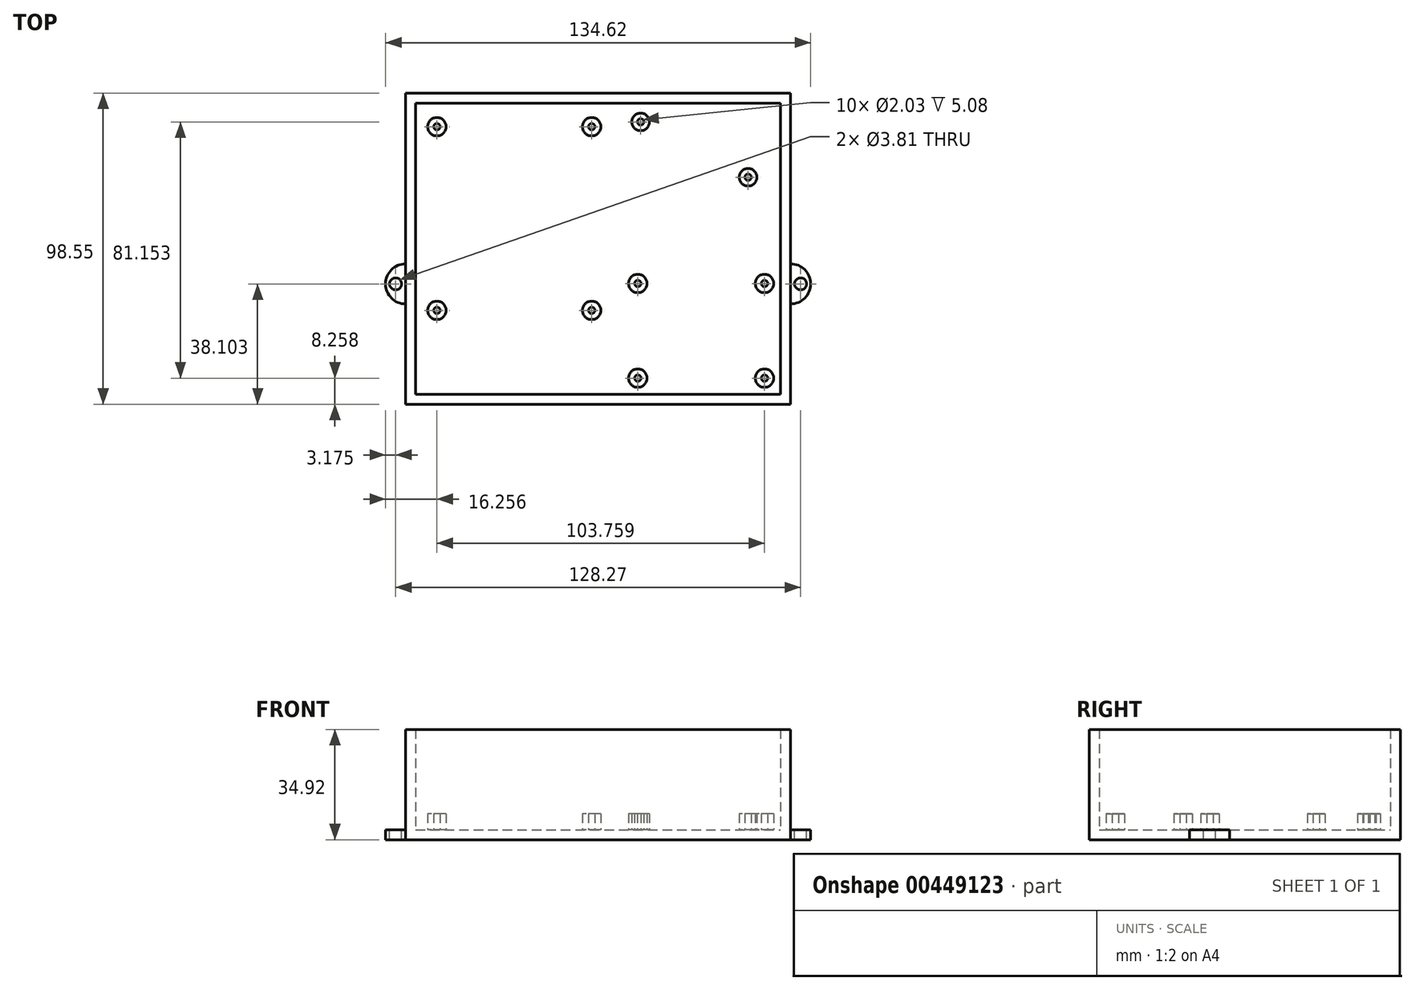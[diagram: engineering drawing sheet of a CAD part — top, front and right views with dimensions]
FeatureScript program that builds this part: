
annotation { "Feature Type Name" : "Feature", "Feature Type Description" : "" }
export const myFeature = defineFeature(function(context is Context, id is Id, definition is map)
    precondition{}
    {
        {
            var Q0;
            Q0=qCreatedBy(makeId("Top.planeOp"),FACE);
            var sketch = newSketch(context, id + "F0", { "sketchPlane" : qUnion([Q0])});
            skLineSegment(sketch, "E0.bottom", {"start": v(-73.66, 41.28) * mm, "end": v(48.26, 41.28) * mm});
            skLineSegment(sketch, "E0.top", {"start": v(-73.66, -57.28) * mm, "end": v(48.26, -57.28) * mm});
            skLineSegment(sketch, "E0.left", {"start": v(-73.66, 41.28) * mm, "end": v(-73.66, -57.28) * mm});
            skLineSegment(sketch, "E0.right", {"start": v(48.26, 41.28) * mm, "end": v(48.26, -57.28) * mm});
            skSolve(sketch);
        }
        {
            var Q0;
            Q0=makeQuery(id+"F0.imprint","IMPRINT",FACE,{"disambiguationData":[TD([[makeQuery(id+"F0.imprint","IMPRINT",EDGE,{"derivedFrom":sQuery(id+"F0.wireOp",EDGE,"E0.bottom")}),-1.0]])]});
            extrude(context, id + "F1", {"entities" : qUnion([Q0]), "depth" : 3.17 * mm});
        }
        {
            var Q0;
            Q0=makeQuery(id+"F1.opExtrude","SWEPT_FACE",FACE,{"disambiguationData":[OSD([sQuery(id+"F0.wireOp",EDGE,"E0.right")])]});
            var sketch = newSketch(context, id + "F2", { "sketchPlane" : qUnion([Q0])});
            skLineSegment(sketch, "E1.bottom", {"start": v(-25.53, 0) * mm, "end": v(-12.83, 0) * mm});
            skLineSegment(sketch, "E1.top", {"start": v(-25.53, 3.17) * mm, "end": v(-12.83, 3.17) * mm});
            skLineSegment(sketch, "E1.left", {"start": v(-25.53, 0) * mm, "end": v(-25.53, 3.17) * mm});
            skLineSegment(sketch, "E1.right", {"start": v(-12.83, 0) * mm, "end": v(-12.83, 3.17) * mm});
            skLineSegment(sketch, "E2", {"start": v(-25.53, 0) * mm, "end": v(-57.28, 0) * mm, "construction": true});
            skSolve(sketch);
        }
        {
            var Q0;
            Q0=makeQuery(id+"F2.imprint","IMPRINT",FACE,{"disambiguationData":[TD([[makeQuery(id+"F2.imprint","IMPRINT",EDGE,{"derivedFrom":sQuery(id+"F2.wireOp",EDGE,"E1.bottom")}),-1.0]])]});
            extrude(context, id + "F3", {"entities" : qUnion([Q0]), "operationType" : NewBodyOperationType.ADD, "depth" : 6.35 * mm});
        }
        {
            var Q0;
            Q0=makeQuery(id+"F1.opExtrude","SWEPT_FACE",FACE,{"disambiguationData":[OSD([sQuery(id+"F0.wireOp",EDGE,"E0.left")])]});
            var sketch = newSketch(context, id + "F4", { "sketchPlane" : qUnion([Q0])});
            skLineSegment(sketch, "E3.bottom", {"start": v(12.83, 0) * mm, "end": v(25.53, 0) * mm});
            skLineSegment(sketch, "E3.top", {"start": v(12.83, 3.18) * mm, "end": v(25.53, 3.18) * mm});
            skLineSegment(sketch, "E3.left", {"start": v(12.83, 0) * mm, "end": v(12.83, 3.18) * mm});
            skLineSegment(sketch, "E3.right", {"start": v(25.53, 0) * mm, "end": v(25.53, 3.18) * mm});
            skLineSegment(sketch, "E4", {"start": v(57.28, 0) * mm, "end": v(25.53, 0) * mm, "construction": true});
            skSolve(sketch);
        }
        {
            var Q0;
            Q0=makeQuery(id+"F4.imprint","IMPRINT",FACE,{"disambiguationData":[TD([[makeQuery(id+"F4.imprint","IMPRINT",EDGE,{"derivedFrom":sQuery(id+"F4.wireOp",EDGE,"E3.bottom")}),1.0]])]});
            extrude(context, id + "F5", {"entities" : qUnion([Q0]), "operationType" : NewBodyOperationType.ADD, "depth" : 6.35 * mm});
        }
        {
            var Q0;
            Q0=makeQuery(id+"FaVg6euIrQHNksh_1.opExtrude","CAP_EDGE",EDGE,{"disambiguationData":[OSD([sQuery(id+"FkQ3vqy4hY3QKMT_1.wireOp",EDGE,"Yg9sziPS-2V4h-UQLX-E8gU-2OajwgteZGGz.right")])],"isStart":false});
            var Q1;
            Q1=makeQuery(id+"FaVg6euIrQHNksh_1.opExtrude","CAP_EDGE",EDGE,{"disambiguationData":[OSD([sQuery(id+"FkQ3vqy4hY3QKMT_1.wireOp",EDGE,"Yg9sziPS-2V4h-UQLX-E8gU-2OajwgteZGGz.left")])],"isStart":false});
            var Q2;
            Q2=makeQuery(id+"FaVg6euIrQHNksh_1.opExtrude","CAP_EDGE",EDGE,{"disambiguationData":[OSD([sQuery(id+"FkQ3vqy4hY3QKMT_1.wireOp",EDGE,"JQurt5le-ksY8-GB8i-C2E5-fmt823hqq3je.right")])],"isStart":false});
            var Q3;
            Q3=makeQuery(id+"FaVg6euIrQHNksh_1.opExtrude","CAP_EDGE",EDGE,{"disambiguationData":[OSD([sQuery(id+"FkQ3vqy4hY3QKMT_1.wireOp",EDGE,"JQurt5le-ksY8-GB8i-C2E5-fmt823hqq3je.left")])],"isStart":false});
            var Q4;
            Q4=makeQuery(id+"F5.opExtrude","CAP_EDGE",EDGE,{"disambiguationData":[OSD([sQuery(id+"F4.wireOp",EDGE,"E3.right")])],"isStart":false});
            var Q5;
            Q5=makeQuery(id+"F5.opExtrude","CAP_EDGE",EDGE,{"disambiguationData":[OSD([sQuery(id+"F4.wireOp",EDGE,"E3.left")])],"isStart":false});
            var Q6;
            Q6=makeQuery(id+"F3.opExtrude","CAP_EDGE",EDGE,{"disambiguationData":[OSD([sQuery(id+"F2.wireOp",EDGE,"E1.left")])],"isStart":false});
            var Q7;
            Q7=makeQuery(id+"F3.opExtrude","CAP_EDGE",EDGE,{"disambiguationData":[OSD([sQuery(id+"F2.wireOp",EDGE,"E1.right")])],"isStart":false});
            fillet(context, id + "F6", {"entities" : qUnion([Q0, Q1, Q2, Q3, Q4, Q5, Q6, Q7]), "radius" : 6.35 * mm, "tangentPropagation" : true, "allowEdgeOverflow" : false});
        }
        {
            var Q0;
            {var subQ2=sQuery(id+"FBJeiMYnQQNTDJ8_1.wireOp",EDGE,"NU6RmQLN-OpBs-DRR8-WLyE-sT2VYZkfqMhq.right");var subQ3=makeQuery(id+"F1.opExtrude","SWEPT_FACE",FACE,{"disambiguationData":[OSD([subQ2])]});var subQ5=sQuery(id+"F2.wireOp",EDGE,"E1.top");var subQ11=sQuery(id+"FBJeiMYnQQNTDJ8_1.wireOp",EDGE,"NU6RmQLN-OpBs-DRR8-WLyE-sT2VYZkfqMhq.left");var subQ12=sQuery(id+"FBJeiMYnQQNTDJ8_1.wireOp",EDGE,"NU6RmQLN-OpBs-DRR8-WLyE-sT2VYZkfqMhq.bottom");var subQ13=sQuery(id+"FBJeiMYnQQNTDJ8_1.wireOp",EDGE,"NU6RmQLN-OpBs-DRR8-WLyE-sT2VYZkfqMhq.top");var subQ14=sQuery(id+"F4.wireOp",EDGE,"E3.top");Q0=makeQuery(id+"Fuqd1rwQzSbVv2O_1.boolean.opBoolean","SPLIT",FACE,{"disambiguationData":[TD([subQ3])],"derivedFrom":makeQuery(id+"F2G8V8C4itq5gVN_1.boolean.opBoolean","SPLIT",FACE,{"disambiguationData":[TD([makeQuery(id+"FTzhnSVDk6kkX89_0.opExtrude","SWEPT_FACE",FACE,{"disambiguationData":[OSD([sQuery(id+"F0IJRBmxtiezRhW_0.wireOp",EDGE,"C5BwnNIY-jE5H-Hf46-yxJA-r1WcZ6m8hW8I.bottom")])]})])],"derivedFrom":makeQuery(id+"F5.boolean.opBoolean","MERGE",FACE,{"derivedFrom":[makeQuery(id+"F3.boolean.opBoolean","MERGE",FACE,{"derivedFrom":[makeQuery(id+"F1.opExtrude","CAP_FACE",FACE,{"disambiguationData":[OSD([subQ12,subQ13,subQ11,subQ2])],"isStart":false}),makeQuery(id+"F3.opExtrude","SWEPT_FACE",FACE,{"disambiguationData":[OSD([subQ5])]})]}),makeQuery(id+"F5.opExtrude","SWEPT_FACE",FACE,{"disambiguationData":[OSD([subQ14])]})]})})});}
            var sketch = newSketch(context, id + "F7", { "sketchPlane" : qUnion([Q0])});
            skCircle(sketch, "E5", {"center": v(51.44, -19.18) * mm, "radius": 1.9 * mm});
            skLineSegment(sketch, "E6", {"start": v(-80, -19.18) * mm, "end": v(-73.66, -19.18) * mm, "construction": true});
            skCircle(sketch, "E7", {"center": v(-76.83, -19.18) * mm, "radius": 1.9 * mm});
            skLineSegment(sketch, "E8", {"start": v(54.61, -19.18) * mm, "end": v(48.26, -19.18) * mm, "construction": true});
            skLineSegment(sketch, "E9", {"start": v(48.26, -12.83) * mm, "end": v(48.26, -25.53) * mm, "construction": true});
            skSolve(sketch);
        }
        {
            var Q0;
            Q0=makeQuery(id+"F7.imprint","IMPRINT",FACE,{"disambiguationData":[TD([[makeQuery(id+"F7.imprint","IMPRINT",EDGE,{"derivedFrom":sQuery(id+"F7.wireOp",EDGE,"E7")}),1.0]])]});
            var Q1;
            Q1=makeQuery(id+"F7.imprint","IMPRINT",FACE,{"disambiguationData":[TD([[makeQuery(id+"F7.imprint","IMPRINT",EDGE,{"derivedFrom":sQuery(id+"F7.wireOp",EDGE,"E5")}),1.0]])]});
            extrude(context, id + "F8", {"entities" : qUnion([Q0, Q1]), "operationType" : NewBodyOperationType.REMOVE, "oppositeDirection" : true, "depth" : 6.35 * mm});
        }
        {
            var Q0;
            Q0=makeQuery(id+"F7.imprint","IMPRINT",FACE,{"disambiguationData":[TD([[makeQuery(id+"F7.imprint","IMPRINT",EDGE,{"derivedFrom":sQuery(id+"F7.wireOp",EDGE,"E5")}),-1.0]])]});
            var sketch = newSketch(context, id + "F9", { "sketchPlane" : qUnion([Q0])});
            skLineSegment(sketch, "E10.bottom", {"start": v(48.26, -57.28) * mm, "end": v(45.09, -57.28) * mm});
            skLineSegment(sketch, "E10.top", {"start": v(48.26, 41.28) * mm, "end": v(45.08, 41.28) * mm});
            skLineSegment(sketch, "E10.left", {"start": v(48.26, -57.28) * mm, "end": v(48.26, 41.28) * mm});
            skLineSegment(sketch, "E10.right", {"start": v(45.09, -57.28) * mm, "end": v(45.08, 41.28) * mm});
            skLineSegment(sketch, "E11.bottom", {"start": v(-73.66, -57.28) * mm, "end": v(-70.49, -57.28) * mm});
            skLineSegment(sketch, "E11.top", {"start": v(-73.66, 41.27) * mm, "end": v(-70.49, 41.27) * mm});
            skLineSegment(sketch, "E11.left", {"start": v(-73.66, -57.28) * mm, "end": v(-73.66, 41.28) * mm});
            skLineSegment(sketch, "E11.right", {"start": v(-70.49, -57.28) * mm, "end": v(-70.49, 41.28) * mm});
            skLineSegment(sketch, "E12.bottom", {"start": v(-70.49, -57.28) * mm, "end": v(45.09, -57.28) * mm});
            skLineSegment(sketch, "E12.top", {"start": v(-70.49, -54.1) * mm, "end": v(45.09, -54.1) * mm});
            skLineSegment(sketch, "E12.left", {"start": v(-70.49, -57.28) * mm, "end": v(-70.49, -54.1) * mm});
            skLineSegment(sketch, "E12.right", {"start": v(45.09, -57.28) * mm, "end": v(45.09, -54.1) * mm});
            skLineSegment(sketch, "E13.bottom", {"start": v(45.08, 41.28) * mm, "end": v(-70.49, 41.27) * mm});
            skLineSegment(sketch, "E13.top", {"start": v(45.08, 38.1) * mm, "end": v(-70.49, 38.1) * mm});
            skLineSegment(sketch, "E13.left", {"start": v(45.08, 41.28) * mm, "end": v(45.08, 38.1) * mm});
            skLineSegment(sketch, "E13.right", {"start": v(-70.49, 41.28) * mm, "end": v(-70.49, 38.1) * mm});
            skSolve(sketch);
        }
        {
            var Q0;
            {var subQ5=sQuery(id+"F9.wireOp",EDGE,"E11.bottom");Q0=makeQuery(id+"F9.imprint","IMPRINT",FACE,{"disambiguationData":[TD([[makeQuery(id+"F9.imprint","IMPRINT",EDGE,{"derivedFrom":subQ5}),1.0]])]});}
            var Q1;
            Q1=makeQuery(id+"F9.imprint","IMPRINT",FACE,{"disambiguationData":[TD([[makeQuery(id+"F9.imprint","IMPRINT",EDGE,{"derivedFrom":sQuery(id+"F9.wireOp",EDGE,"E12.bottom")}),1.0]])]});
            var Q2;
            Q2=makeQuery(id+"F9.imprint","IMPRINT",FACE,{"disambiguationData":[TD([[makeQuery(id+"F9.imprint","IMPRINT",EDGE,{"derivedFrom":sQuery(id+"F9.wireOp",EDGE,"E13.bottom")}),-1.0]])]});
            var Q3;
            {var subQ5=sQuery(id+"F9.wireOp",EDGE,"E10.bottom");Q3=makeQuery(id+"F9.imprint","IMPRINT",FACE,{"disambiguationData":[TD([[makeQuery(id+"F9.imprint","IMPRINT",EDGE,{"derivedFrom":subQ5}),1.0]])]});}
            extrude(context, id + "F10", {"entities" : qUnion([Q0, Q1, Q2, Q3]), "operationType" : NewBodyOperationType.ADD, "depth" : 31.75 * mm});
        }
        {
            var Q0;
            Q0=makeQuery(id+"F10.boolean.opBoolean","SPLIT",FACE,{"disambiguationData":[TD([makeQuery(id+"F10.opExtrude","SWEPT_FACE",FACE,{"disambiguationData":[OSD([sQuery(id+"F9.wireOp",EDGE,"E10.right")])]})])],"derivedFrom":makeQuery(id+"F5.boolean.opBoolean","MERGE",FACE,{"derivedFrom":[makeQuery(id+"F3.boolean.opBoolean","MERGE",FACE,{"derivedFrom":[makeQuery(id+"F1.opExtrude","CAP_FACE",FACE,{"disambiguationData":[OSD([sQuery(id+"F0.wireOp",EDGE,"E0.bottom"),sQuery(id+"F0.wireOp",EDGE,"E0.top"),sQuery(id+"F0.wireOp",EDGE,"E0.left"),sQuery(id+"F0.wireOp",EDGE,"E0.right")])],"isStart":false}),makeQuery(id+"F3.opExtrude","SWEPT_FACE",FACE,{"disambiguationData":[OSD([sQuery(id+"F2.wireOp",EDGE,"E1.top")])]})]}),makeQuery(id+"F5.opExtrude","SWEPT_FACE",FACE,{"disambiguationData":[OSD([sQuery(id+"F4.wireOp",EDGE,"E3.top")])]})]})});
            var sketch = newSketch(context, id + "F11", { "sketchPlane" : qUnion([Q0])});
            skLineSegment(sketch, "E14.bottom", {"start": v(-14.73, 30.6) * mm, "end": v(-14.73, 34.16) * mm, "construction": true});
            skLineSegment(sketch, "E14.top", {"start": v(-11.18, 30.6) * mm, "end": v(-11.18, 34.16) * mm, "construction": true});
            skLineSegment(sketch, "E14.left", {"start": v(-14.73, 30.6) * mm, "end": v(-11.18, 30.6) * mm, "construction": true});
            skLineSegment(sketch, "E14.right", {"start": v(-14.73, 34.16) * mm, "end": v(-11.18, 34.16) * mm, "construction": true});
            skCircle(sketch, "E15", {"center": v(-14.73, 30.6) * mm, "radius": 1.02 * mm});
            skCircle(sketch, "E16", {"center": v(-14.73, 30.6) * mm, "radius": 2.92 * mm});
            skLineSegment(sketch, "E17.bottom", {"start": v(-14.73, 30.6) * mm, "end": v(-14.73, -27.56) * mm, "construction": true});
            skLineSegment(sketch, "E17.top", {"start": v(-63.75, 30.6) * mm, "end": v(-63.75, -27.56) * mm, "construction": true});
            skLineSegment(sketch, "E17.left", {"start": v(-14.73, 30.6) * mm, "end": v(-63.75, 30.6) * mm, "construction": true});
            skLineSegment(sketch, "E17.right", {"start": v(-14.73, -27.56) * mm, "end": v(-63.75, -27.56) * mm, "construction": true});
            skCircle(sketch, "E18", {"center": v(-63.75, -27.56) * mm, "radius": 1.02 * mm});
            skCircle(sketch, "E19", {"center": v(-63.75, -27.56) * mm, "radius": 2.92 * mm});
            skCircle(sketch, "E20", {"center": v(-63.75, 30.6) * mm, "radius": 1.02 * mm});
            skCircle(sketch, "E21", {"center": v(-63.75, 30.6) * mm, "radius": 2.92 * mm});
            skCircle(sketch, "E22", {"center": v(-14.73, -27.56) * mm, "radius": 1.02 * mm});
            skCircle(sketch, "E23", {"center": v(-14.73, -27.56) * mm, "radius": 2.92 * mm});
            skLineSegment(sketch, "E24.bottom", {"start": v(-11.18, 34.16) * mm, "end": v(-11.18, -50.93) * mm, "construction": true});
            skLineSegment(sketch, "E24.top", {"start": v(-67.31, 34.16) * mm, "end": v(-67.31, -50.93) * mm, "construction": true});
            skLineSegment(sketch, "E24.left", {"start": v(-11.18, 34.16) * mm, "end": v(-67.31, 34.16) * mm, "construction": true});
            skLineSegment(sketch, "E24.right", {"start": v(-11.18, -50.93) * mm, "end": v(-67.31, -50.93) * mm, "construction": true});
            skLineSegment(sketch, "E25.bottom", {"start": v(-70.49, -54.1) * mm, "end": v(-67.31, -54.1) * mm, "construction": true});
            skLineSegment(sketch, "E25.top", {"start": v(-70.49, -50.93) * mm, "end": v(-67.31, -50.93) * mm, "construction": true});
            skLineSegment(sketch, "E25.left", {"start": v(-70.49, -54.1) * mm, "end": v(-70.49, -50.93) * mm, "construction": true});
            skLineSegment(sketch, "E25.right", {"start": v(-67.31, -54.1) * mm, "end": v(-67.31, -50.93) * mm, "construction": true});
            skSolve(sketch);
        }
        {
            var Q0;
            Q0=makeQuery(id+"F11.imprint","IMPRINT",FACE,{"disambiguationData":[TD([[makeQuery(id+"F11.imprint","IMPRINT",EDGE,{"derivedFrom":sQuery(id+"F11.wireOp",EDGE,"E16")}),-1.0]])]});
            var sketch = newSketch(context, id + "F12", { "sketchPlane" : qUnion([Q0])});
            skLineSegment(sketch, "E26.bottom", {"start": v(34.8, 11.81) * mm, "end": v(41.9, 11.81) * mm, "construction": true});
            skLineSegment(sketch, "E26.top", {"start": v(34.8, 14.6) * mm, "end": v(41.9, 14.6) * mm, "construction": true});
            skLineSegment(sketch, "E26.left", {"start": v(34.8, 11.81) * mm, "end": v(34.8, 14.6) * mm, "construction": true});
            skLineSegment(sketch, "E26.right", {"start": v(41.9, 11.81) * mm, "end": v(41.9, 14.6) * mm, "construction": true});
            skCircle(sketch, "E27", {"center": v(34.8, 14.6) * mm, "radius": 1.02 * mm});
            skCircle(sketch, "E28", {"center": v(34.8, 14.6) * mm, "radius": 2.8 * mm});
            skLineSegment(sketch, "E29.bottom", {"start": v(34.8, 14.6) * mm, "end": v(0.76, 14.6) * mm, "construction": true});
            skLineSegment(sketch, "E29.top", {"start": v(34.8, 32.13) * mm, "end": v(0.76, 32.13) * mm, "construction": true});
            skLineSegment(sketch, "E29.left", {"start": v(34.8, 14.6) * mm, "end": v(34.8, 32.13) * mm, "construction": true});
            skLineSegment(sketch, "E29.right", {"start": v(0.76, 14.6) * mm, "end": v(0.76, 32.13) * mm, "construction": true});
            skCircle(sketch, "E30", {"center": v(0.76, 32.13) * mm, "radius": 1.02 * mm});
            skCircle(sketch, "E31", {"center": v(0.76, 32.13) * mm, "radius": 2.8 * mm});
            skLineSegment(sketch, "E32.bottom", {"start": v(41.9, 11.81) * mm, "end": v(-6.35, 11.81) * mm, "construction": true});
            skLineSegment(sketch, "E32.left", {"start": v(41.9, 11.81) * mm, "end": v(41.9, 34.93) * mm, "construction": true});
            skLineSegment(sketch, "E32.right", {"start": v(-6.35, 11.81) * mm, "end": v(-6.35, 34.93) * mm, "construction": true});
            skLineSegment(sketch, "E33.top", {"start": v(41.9, 34.93) * mm, "end": v(-6.35, 34.93) * mm, "construction": true});
            skLineSegment(sketch, "E34.bottom", {"start": v(0.76, 32.13) * mm, "end": v(-6.35, 32.13) * mm, "construction": true});
            skLineSegment(sketch, "E34.top", {"start": v(0.76, 34.93) * mm, "end": v(-6.35, 34.93) * mm, "construction": true});
            skLineSegment(sketch, "E34.left", {"start": v(0.76, 32.13) * mm, "end": v(0.76, 34.93) * mm, "construction": true});
            skLineSegment(sketch, "E34.right", {"start": v(-6.35, 32.13) * mm, "end": v(-6.35, 34.93) * mm, "construction": true});
            skLineSegment(sketch, "E35", {"start": v(41.91, 34.93) * mm, "end": v(41.91, 38.1) * mm, "construction": true});
            skLineSegment(sketch, "E36", {"start": v(41.9, 34.93) * mm, "end": v(45.08, 34.93) * mm, "construction": true});
            skSolve(sketch);
        }
        {
            var Q0;
            Q0=makeQuery(id+"F11.imprint","IMPRINT",FACE,{"disambiguationData":[TD([[makeQuery(id+"F11.imprint","IMPRINT",EDGE,{"derivedFrom":sQuery(id+"F11.wireOp",EDGE,"E16")}),-1.0]])]});
            var sketch = newSketch(context, id + "F13", { "sketchPlane" : qUnion([Q0])});
            skCircle(sketch, "E37", {"center": v(40, -49.02) * mm, "radius": 2.92 * mm});
            skCircle(sketch, "E38", {"center": v(40, -49.02) * mm, "radius": 1.02 * mm});
            skCircle(sketch, "E39", {"center": v(-0.13, -49.02) * mm, "radius": 2.92 * mm});
            skCircle(sketch, "E40", {"center": v(-0.13, -49.02) * mm, "radius": 1.02 * mm});
            skCircle(sketch, "E41", {"center": v(40, -19.05) * mm, "radius": 2.92 * mm});
            skCircle(sketch, "E42", {"center": v(40, -19.05) * mm, "radius": 1.02 * mm});
            skCircle(sketch, "E43", {"center": v(-0.13, -19.05) * mm, "radius": 2.92 * mm});
            skCircle(sketch, "E44", {"center": v(-0.13, -19.05) * mm, "radius": 1.02 * mm});
            skLineSegment(sketch, "E45", {"start": v(40, -49.02) * mm, "end": v(45.09, -49.02) * mm, "construction": true});
            skLineSegment(sketch, "E46", {"start": v(40, -49.02) * mm, "end": v(40, -54.1) * mm, "construction": true});
            skLineSegment(sketch, "E47", {"start": v(40, -49.02) * mm, "end": v(40, -19.05) * mm, "construction": true});
            skLineSegment(sketch, "E48", {"start": v(40, -19.05) * mm, "end": v(-0.13, -19.05) * mm, "construction": true});
            skLineSegment(sketch, "E49", {"start": v(-0.13, -19.05) * mm, "end": v(-0.13, -49.02) * mm, "construction": true});
            skLineSegment(sketch, "E50", {"start": v(40, -49.02) * mm, "end": v(-0.13, -49.02) * mm, "construction": true});
            skSolve(sketch);
        }
        {
            var Q0;
            Q0=makeQuery(id+"F11.imprint","IMPRINT",FACE,{"disambiguationData":[TD([[makeQuery(id+"F11.imprint","IMPRINT",EDGE,{"derivedFrom":sQuery(id+"F11.wireOp",EDGE,"E20")}),-1.0]])]});
            var Q1;
            Q1=makeQuery(id+"F11.imprint","IMPRINT",FACE,{"disambiguationData":[TD([[makeQuery(id+"F11.imprint","IMPRINT",EDGE,{"derivedFrom":sQuery(id+"F11.wireOp",EDGE,"E22")}),-1.0]])]});
            var Q2;
            Q2=makeQuery(id+"F11.imprint","IMPRINT",FACE,{"disambiguationData":[TD([[makeQuery(id+"F11.imprint","IMPRINT",EDGE,{"derivedFrom":sQuery(id+"F11.wireOp",EDGE,"E15")}),-1.0]])]});
            var Q3;
            Q3=makeQuery(id+"F11.imprint","IMPRINT",FACE,{"disambiguationData":[TD([[makeQuery(id+"F11.imprint","IMPRINT",EDGE,{"derivedFrom":sQuery(id+"F11.wireOp",EDGE,"E18")}),-1.0]])]});
            var Q4;
            Q4=makeQuery(id+"F12.imprint","IMPRINT",FACE,{"disambiguationData":[TD([[makeQuery(id+"F12.imprint","IMPRINT",EDGE,{"derivedFrom":sQuery(id+"F12.wireOp",EDGE,"E27")}),-1.0]])]});
            var Q5;
            Q5=makeQuery(id+"F12.imprint","IMPRINT",FACE,{"disambiguationData":[TD([[makeQuery(id+"F12.imprint","IMPRINT",EDGE,{"derivedFrom":sQuery(id+"F12.wireOp",EDGE,"E30")}),-1.0]])]});
            var Q6;
            Q6=makeQuery(id+"F13.imprint","IMPRINT",FACE,{"disambiguationData":[TD([[makeQuery(id+"F13.imprint","IMPRINT",EDGE,{"derivedFrom":sQuery(id+"F13.wireOp",EDGE,"E41")}),1.0]])]});
            var Q7;
            Q7=makeQuery(id+"F13.imprint","IMPRINT",FACE,{"disambiguationData":[TD([[makeQuery(id+"F13.imprint","IMPRINT",EDGE,{"derivedFrom":sQuery(id+"F13.wireOp",EDGE,"E37")}),1.0]])]});
            var Q8;
            Q8=makeQuery(id+"F13.imprint","IMPRINT",FACE,{"disambiguationData":[TD([[makeQuery(id+"F13.imprint","IMPRINT",EDGE,{"derivedFrom":sQuery(id+"F13.wireOp",EDGE,"E39")}),1.0]])]});
            var Q9;
            Q9=makeQuery(id+"F13.imprint","IMPRINT",FACE,{"disambiguationData":[TD([[makeQuery(id+"F13.imprint","IMPRINT",EDGE,{"derivedFrom":sQuery(id+"F13.wireOp",EDGE,"E43")}),1.0]])]});
            extrude(context, id + "F14", {"entities" : qUnion([Q0, Q1, Q2, Q3, Q4, Q5, Q6, Q7, Q8, Q9]), "operationType" : NewBodyOperationType.ADD, "depth" : 5.08 * mm});
        }
    });
